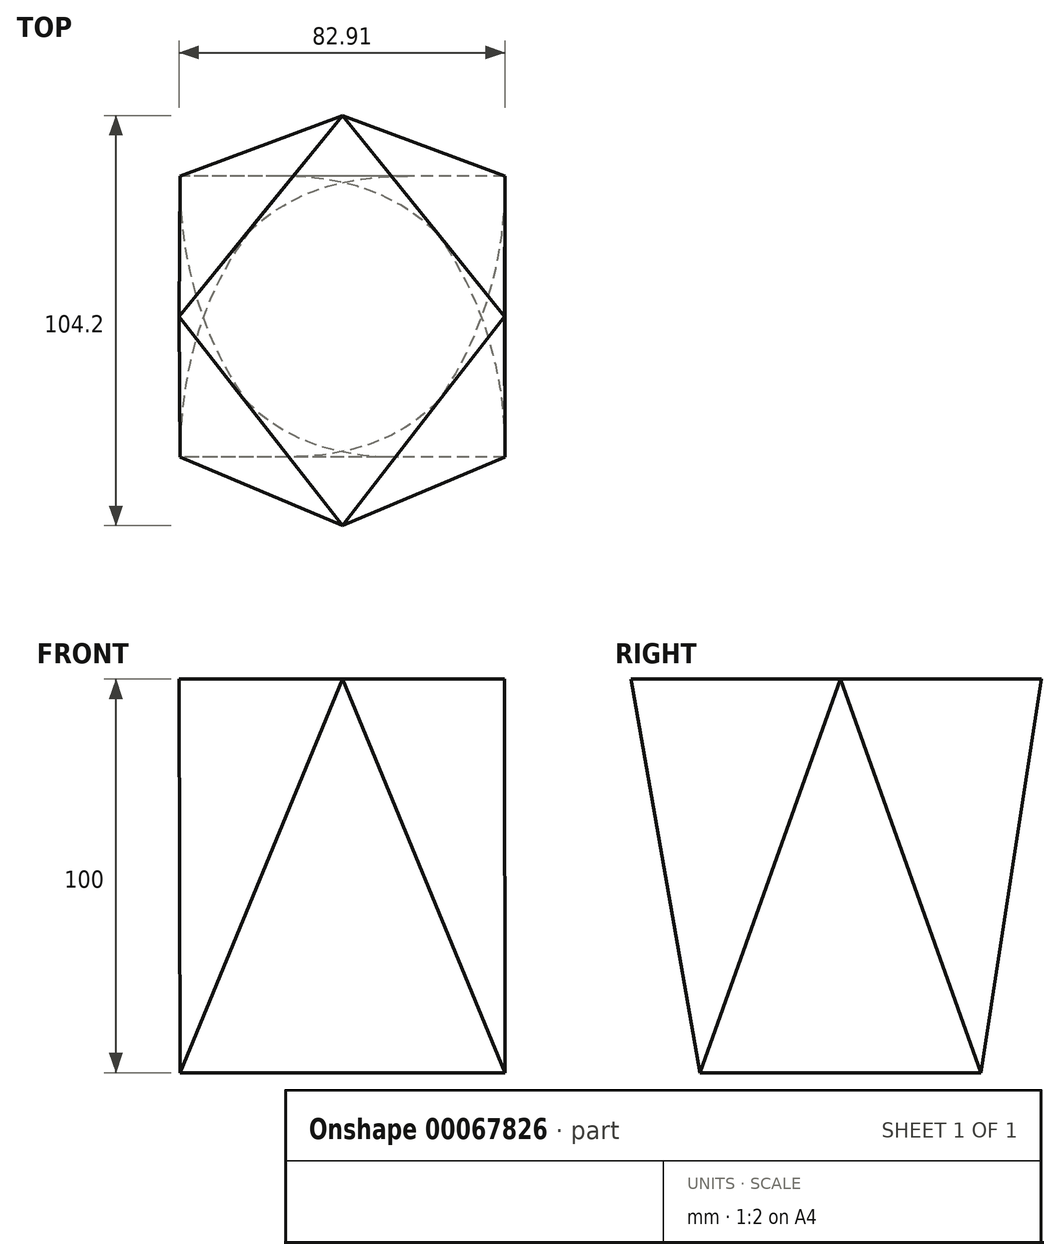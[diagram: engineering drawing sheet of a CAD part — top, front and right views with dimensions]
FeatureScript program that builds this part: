
annotation { "Feature Type Name" : "Feature", "Feature Type Description" : "" }
export const myFeature = defineFeature(function(context is Context, id is Id, definition is map)
    precondition{}
    {
        {
            var Q0;
            Q0=qCreatedBy(makeId("Top.planeOp"),FACE);
            var sketch = newSketch(context, id + "F0", { "sketchPlane" : qUnion([Q0])});
            skLineSegment(sketch, "E0.rect.bottom", {"start": v(41.28, -35.69) * mm, "end": v(-41.28, -35.69) * mm});
            skLineSegment(sketch, "E0.rect.top", {"start": v(41.28, 35.69) * mm, "end": v(-41.28, 35.69) * mm});
            skLineSegment(sketch, "E0.rect.left", {"start": v(41.28, -35.69) * mm, "end": v(41.28, 35.69) * mm});
            skLineSegment(sketch, "E0.rect.right", {"start": v(-41.28, -35.69) * mm, "end": v(-41.28, 35.69) * mm});
            skPoint(sketch, "E0.rect.middle", {"position": v(0, 0) * mm});
            skSolve(sketch);
        }
        {
            var Q0;
            Q0=qCreatedBy(makeId("Top.planeOp"),FACE);
            cPlane(context, id + "F1", {"entities" : qUnion([Q0]), "cplaneType" : CPlaneType.OFFSET, "offset" : 100 * mm, "width" : 150 * mm, "height" : 150 * mm});
        }
        {
            var Q0;
            Q0=qCreatedBy(id+"F1.planeOp",FACE);
            var sketch = newSketch(context, id + "F2", { "sketchPlane" : qUnion([Q0])});
            skLineSegment(sketch, "E1", {"start": v(0, 51.05) * mm, "end": v(-41.63, 0) * mm});
            skLineSegment(sketch, "E2", {"start": v(-41.63, 0) * mm, "end": v(0, -53.15) * mm});
            skLineSegment(sketch, "E3", {"start": v(0, -53.15) * mm, "end": v(41.1, 0) * mm});
            skLineSegment(sketch, "E4", {"start": v(41.1, 0) * mm, "end": v(0, 51.05) * mm});
            skSolve(sketch);
        }
        {
            var Q0;
            Q0=makeQuery(id+"F0.imprint","IMPRINT",FACE,{"disambiguationData":[TD([[makeQuery(id+"F0.imprint","IMPRINT",EDGE,{"derivedFrom":sQuery(id+"F0.wireOp",EDGE,"E0.rect.bottom")}),-1.0]])]});
            var Q1;
            Q1=makeQuery(id+"F2.imprint","IMPRINT",FACE,{"disambiguationData":[TD([[makeQuery(id+"F2.imprint","IMPRINT",EDGE,{"derivedFrom":sQuery(id+"F2.wireOp",EDGE,"E1")}),1.0]])]});
            var Q2;
            Q2=sQuery(id+"F0.wireOp",VERTEX,"E0.rect.right.start");
            var Q3;
            Q3=sQuery(id+"F2.wireOp",VERTEX,"E2.start");
            loft(context, id + "F3", {"sheetProfilesArray" : [{ "sheetProfileEntities" : qUnion([Q0]) }, { "sheetProfileEntities" : qUnion([Q1]) }], "matchConnections" : true, "connections" : [{ "connectionEntities" : qUnion([Q2, Q3]), "connectionEdgeQueries" : qUnion([]), "connectionEdgeParameters" : [] }]});
        }
        {
            var Q0;
            Q0=makeQuery(id+"F0.imprint","IMPRINT",FACE,{"disambiguationData":[TD([[makeQuery(id+"F0.imprint","IMPRINT",EDGE,{"derivedFrom":sQuery(id+"F0.wireOp",EDGE,"E0.rect.bottom")}),-1.0]])]});
            var Q1;
            Q1=makeQuery(id+"F2.imprint","IMPRINT",FACE,{"disambiguationData":[TD([[makeQuery(id+"F2.imprint","IMPRINT",EDGE,{"derivedFrom":sQuery(id+"F2.wireOp",EDGE,"E1")}),1.0]])]});
            var Q2;
            Q2=sQuery(id+"F0.wireOp",VERTEX,"E0.rect.right.start");
            var Q3;
            Q3=sQuery(id+"F2.wireOp",VERTEX,"E3.start");
            loft(context, id + "F4", {"sheetProfilesArray" : [{ "sheetProfileEntities" : qUnion([Q0]) }, { "sheetProfileEntities" : qUnion([Q1]) }], "matchConnections" : true, "connections" : [{ "connectionEntities" : qUnion([Q2, Q3]), "connectionEdgeQueries" : qUnion([]), "connectionEdgeParameters" : [] }]});
        }
    });
